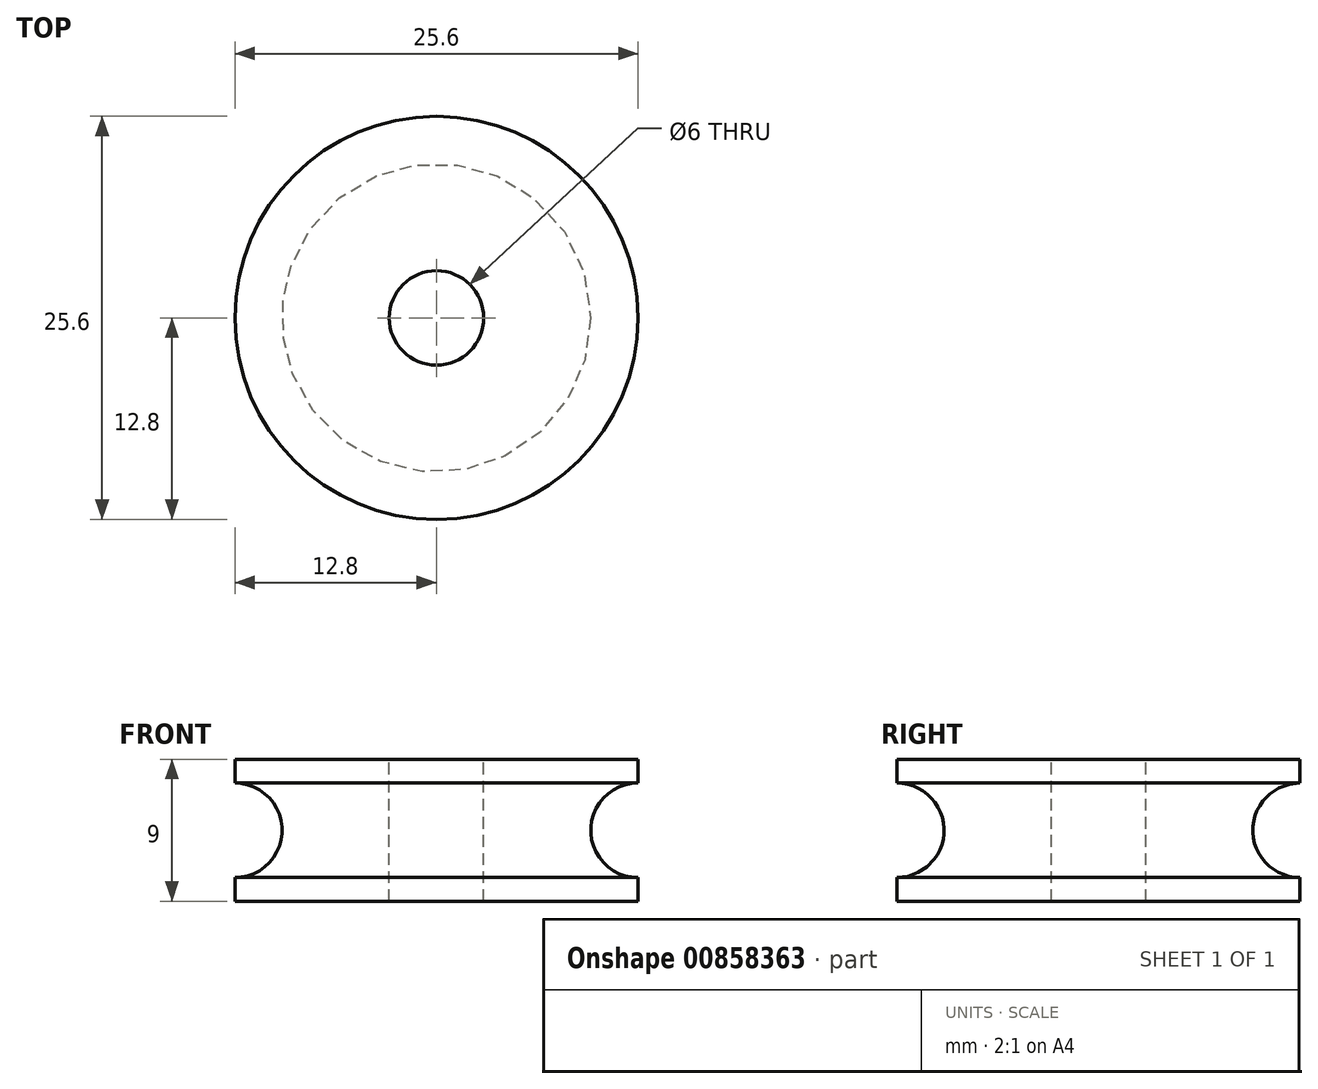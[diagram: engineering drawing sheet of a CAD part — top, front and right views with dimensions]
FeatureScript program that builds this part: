
annotation { "Feature Type Name" : "Feature", "Feature Type Description" : "" }
export const myFeature = defineFeature(function(context is Context, id is Id, definition is map)
    precondition{}
    {
        {
            var Q0;
            Q0=qCreatedBy(makeId("Front.planeOp"),FACE);
            var sketch = newSketch(context, id + "F0", { "sketchPlane" : qUnion([Q0])});
            skLineSegment(sketch, "E0", {"start": v(-3, -4.5) * mm, "end": v(-3, 4.5) * mm});
            skLineSegment(sketch, "E1", {"start": v(-3, 4.5) * mm, "end": v(-12.8, 4.5) * mm});
            skLineSegment(sketch, "E2", {"start": v(-12.8, 4.5) * mm, "end": v(-12.8, 3) * mm});
            skLineSegment(sketch, "E3", {"start": v(-12.8, -3) * mm, "end": v(-12.8, -4.5) * mm});
            skLineSegment(sketch, "E4", {"start": v(-12.8, -4.5) * mm, "end": v(-3, -4.5) * mm});
            skCircle(sketch, "E5", {"center": v(-12.8, 0) * mm, "radius": 3 * mm, "construction": true});
            skLineSegment(sketch, "E6", {"start": v(0, 0) * mm, "end": v(0, -16.78) * mm, "construction": true});
            skArc(sketch, "E7", {"start": v(-12.8, 3) * mm, "mid": v(-9.8, 0) * mm, "end": v(-12.8, -3) * mm});
            skSolve(sketch);
        }
        {
            var Q0;
            Q0=makeQuery(id+"F0.imprint","IMPRINT",FACE,{"disambiguationData":[TD([[makeQuery(id+"F0.imprint","IMPRINT",EDGE,{"derivedFrom":sQuery(id+"F0.wireOp",EDGE,"E0")}),1.0]])]});
            var Q1;
            Q1=sQuery(id+"F0.wireOp",EDGE,"E6");
            var Q2;
            Q2=sQuery(id+"F0.wireOp",EDGE,"E6");
            revolve(context, id + "F1", {"surfaceOperationType" : NewSurfaceOperationType.NEW, "entities" : qUnion([Q0]), "surfaceEntities" : qUnion([Q1]), "axis" : qUnion([Q2]), "revolveType" : RevolveType.FULL});
        }
    });
